# Revit family: 0030320
name_source: partatom
category: Lighting Fixtures
revit_build: Autodesk Revit 2017 (Build: 20190507_1515(x64)
units: mm (PartAtom-declared; Revit-internal decimal feet)

## family parameters
Cut with Voids When Loaded = No
Host = Face
Light Source = Yes
OmniClass Number = 23.80.70.00
OmniClass Title = Lighting
Part Type = Normal
Room Calculation Point = No
Round Connector Dimension = Use Diameter
Shared = No

## types (1)
- 0030320 Insaver Slim U19 IP44 170 PIR 1500lm 830
    Apparent Load = 0 VA
    Assembly Code = D5020200
    AssetType = Fixed
    ClassificationName = Uniclass2015
    ClassificationValue = EF_70_80
    Color Filter = 16777215
    Cost = 0 $
    Default Elevation = 1219 mm
    DiameterRecess_SYL = 186 mm  [stored 0.610236 ft]
    DiameterTopBase_SYL = 186 mm  [stored 0.610236 ft]
    DiameterTop_SYL = 120 mm  [stored 0.393701 ft]
    Diameter_SYL = 211 mm  [stored 0.692257 ft]
    Dimming Lamp Color Temperature Shift = <None>
    DimmingControlOptions = Non dimmable
    DocumentationLiterature = http://www.sylvania-lighting.com
    DurationUnit = hours
    ElectricShockClassification = Class II
    Emit Shape Visible in Rendering = No
    Emit from Circle Diameter = 171 mm  [stored 0.561024 ft]
    ExpectedLife = 50000
    HeightBezel_SYL = 3 mm  [stored 0.00984252 ft]
    Height_SYL = 61 mm  [stored 0.200131 ft]
    IfcExportAs = IfcLightFixtureType
    IfcExportType = IfcLightFixtureType
    ImpactProtectionIndex = IK07
    IngressProtection = IP20/44
    InputNominalFrequency = 50/60 Hz
    InputVoltage = 220-240V~
    Keynote = 16500
    Lamp = LED
    LampColourRenderingIndex = 80
    LampColourTemperature = 3000 K
    LampMacAdamStep = 5
    LampNominalLuminous = 1053 lm
    LampsType = LED
    LightOutputRatio = 100
    LuminousEfficacy = 117 lm/W
    Manufacturer = Feilo Sylvania
    ManufacturerName = Feilo Sylvania
    Material = aluminium housing, polycarbonate diffuser
    Material_1_FEILO = Trim-Sylvania-STARTDownlight-White
    Material_2_FEILO = Diffuser-Sylvania-STARTDownlight
    Material_3_FEILO = Top-Sylvania-STARTDownlight
    Material_4_FEILO = LED-Sylvania-STARTDownlight
    Model = Insaver Slim U19 IP44 170 PIR 1500lm 830
    ModelNumber = 0030320
    ModelReference = Insaver Slim U19 IP44 170 PIR 1500lm 830
    Name = Insaver Slim U19 IP44 170 PIR 1500lm 830
    NominalDepth = 61 mm  [stored 0.200131 ft]
    NominalHeight = 175 mm  [stored 0.574147 ft]
    NominalLength = 175 mm  [stored 0.574147 ft]
    Photometric Web File = 0030320.ies
    PowerConsumption = 13.64 W
    PowerFactor = 0.9
    RadiusReflector_SYL = 85 mm  [stored 0.278871 ft]
    RadiusTop_SYL = 6 mm  [stored 0.019685 ft]
    Size1_SYL = No
    Size2_SYL = No
    Size3PIR_SYL = Yes
    Size4_SYL = No
    Tilt Angle = -90.00°
    Type Image = <None>
    TypeName = Insaver Slim U19 IP44 170 PIR 1500lm 830
    URL = http://www.sylvania-lighting.com
    VisibilityPIR_SYL = Yes
    Voltage = 230 V
    WidthBezel_SYL = 30 mm  [stored 0.0984252 ft]

note: [stored X ft] marks values corroborated as IEEE doubles in the binary element streams (Revit-internal decimal feet)

## geometry (parser evidence)
native form markers: Sweep x1
no freeform markers — native parametric forms only
